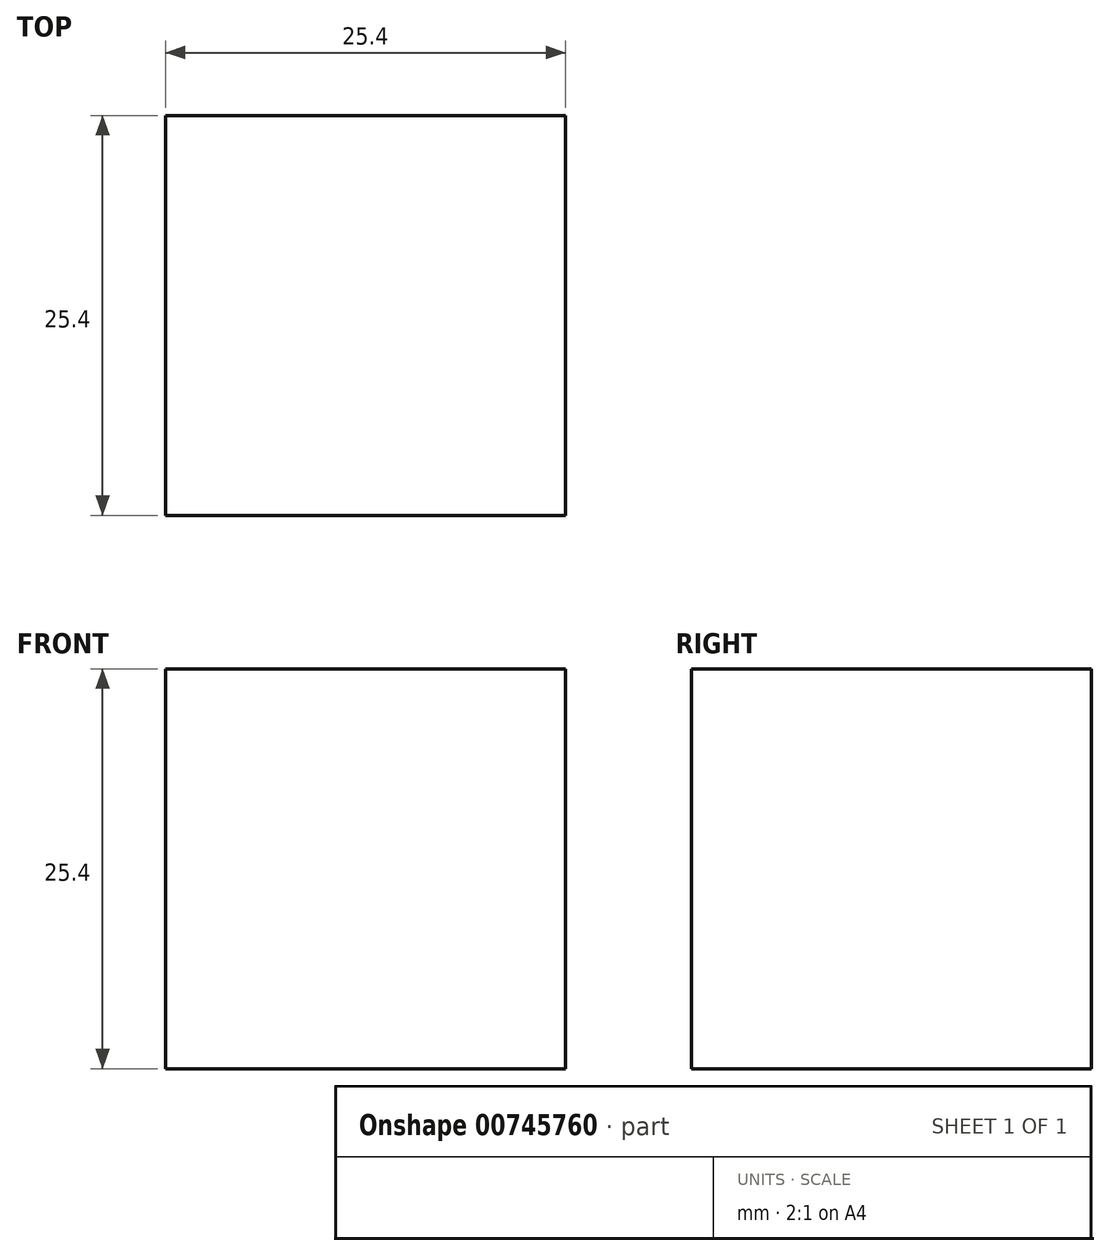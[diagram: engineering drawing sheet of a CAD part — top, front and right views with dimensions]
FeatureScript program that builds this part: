
annotation { "Feature Type Name" : "Feature", "Feature Type Description" : "" }
export const myFeature = defineFeature(function(context is Context, id is Id, definition is map)
    precondition{}
    {
        {
            var Q0;
            Q0=qCreatedBy(makeId("Top.planeOp"),FACE);
            var sketch = newSketch(context, id + "F0", { "sketchPlane" : qUnion([Q0])});
            skLineSegment(sketch, "E0", {"start": v(-55.38, -52.25) * mm, "end": v(-29.98, -52.25) * mm});
            skLineSegment(sketch, "E1", {"start": v(-29.98, -52.25) * mm, "end": v(-29.98, -26.85) * mm});
            skLineSegment(sketch, "E2", {"start": v(-29.98, -26.85) * mm, "end": v(-55.38, -26.85) * mm});
            skLineSegment(sketch, "E3", {"start": v(-55.38, -26.85) * mm, "end": v(-55.38, -52.25) * mm});
            skSolve(sketch);
        }
        {
            var Q0;
            Q0=makeQuery(id+"F0.imprint","IMPRINT",FACE,{"disambiguationData":[TD([[makeQuery(id+"F0.imprint","IMPRINT",EDGE,{"derivedFrom":sQuery(id+"F0.wireOp",EDGE,"E0")}),1.0]])]});
            extrude(context, id + "F1", {"entities" : qUnion([Q0]), "depth" : 25.4 * mm, "offsetDistance" : 25.4 * mm});
        }
    });
